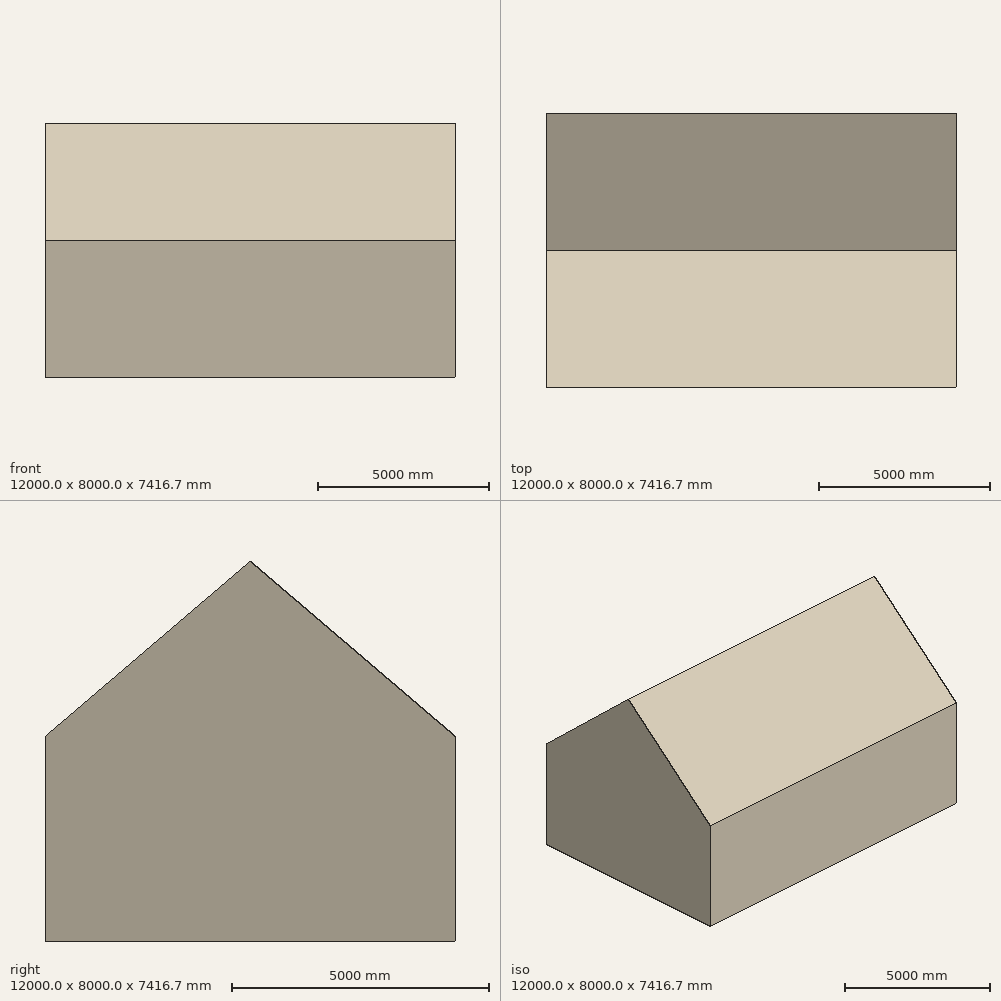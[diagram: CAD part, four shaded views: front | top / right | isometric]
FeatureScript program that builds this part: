
annotation { "Feature Type Name" : "Feature", "Feature Type Description" : "" }
export const myFeature = defineFeature(function(context is Context, id is Id, definition is map)
    precondition{}
    {
        {
            var Q0;
            Q0=qCreatedBy(makeId("Top.planeOp"),FACE);
            var sketch = newSketch(context, id + "F0", { "sketchPlane" : qUnion([Q0])});
            skLineSegment(sketch, "E0.bottom", {"start": v(-5986.09, 5542.23) * mm, "end": v(6013.91, 5542.23) * mm});
            skLineSegment(sketch, "E0.top", {"start": v(-5986.09, -2457.77) * mm, "end": v(6013.91, -2457.77) * mm});
            skLineSegment(sketch, "E0.left", {"start": v(-5986.09, 5542.23) * mm, "end": v(-5986.09, -2457.77) * mm});
            skLineSegment(sketch, "E0.right", {"start": v(6013.91, 5542.23) * mm, "end": v(6013.91, -2457.77) * mm});
            skSolve(sketch);
        }
        {
            var Q0;
            Q0=makeQuery(id+"F0.imprint","IMPRINT",FACE,{"disambiguationData":[TD([[makeQuery(id+"F0.imprint","IMPRINT",EDGE,{"derivedFrom":sQuery(id+"F0.wireOp",EDGE,"E0.bottom")}),-1.0]])]});
            extrude(context, id + "F1", {"entities" : qUnion([Q0]), "depth" : 4000 * mm});
        }
        {
            var Q0;
            Q0=makeQuery(id+"F1.opExtrude","SWEPT_FACE",FACE,{"disambiguationData":[OSD([sQuery(id+"F0.wireOp",EDGE,"E0.right")])]});
            var sketch = newSketch(context, id + "F2", { "sketchPlane" : qUnion([Q0])});
            skLineSegment(sketch, "E1", {"start": v(1542.23, 7416.66) * mm, "end": v(-2457.77, 4000) * mm});
            skLineSegment(sketch, "E2", {"start": v(1542.23, 7416.66) * mm, "end": v(5542.23, 4000) * mm});
            skSolve(sketch);
        }
        {
            var Q0;
            Q0 = qSketchRegion(id + "F2", true);
            var Q1;
            Q1=makeQuery(id+"F2.imprint","IMPRINT",FACE,{"disambiguationData":[TD([[makeQuery(id+"F2.imprint","IMPRINT",EDGE,{"derivedFrom":sQuery(id+"F2.wireOp",EDGE,"E1")}),1.0]])]});
            extrude(context, id + "F3", {"entities" : qUnion([Q0, Q1]), "operationType" : NewBodyOperationType.ADD, "oppositeDirection" : true, "depth" : 12000 * mm});
        }
    });
